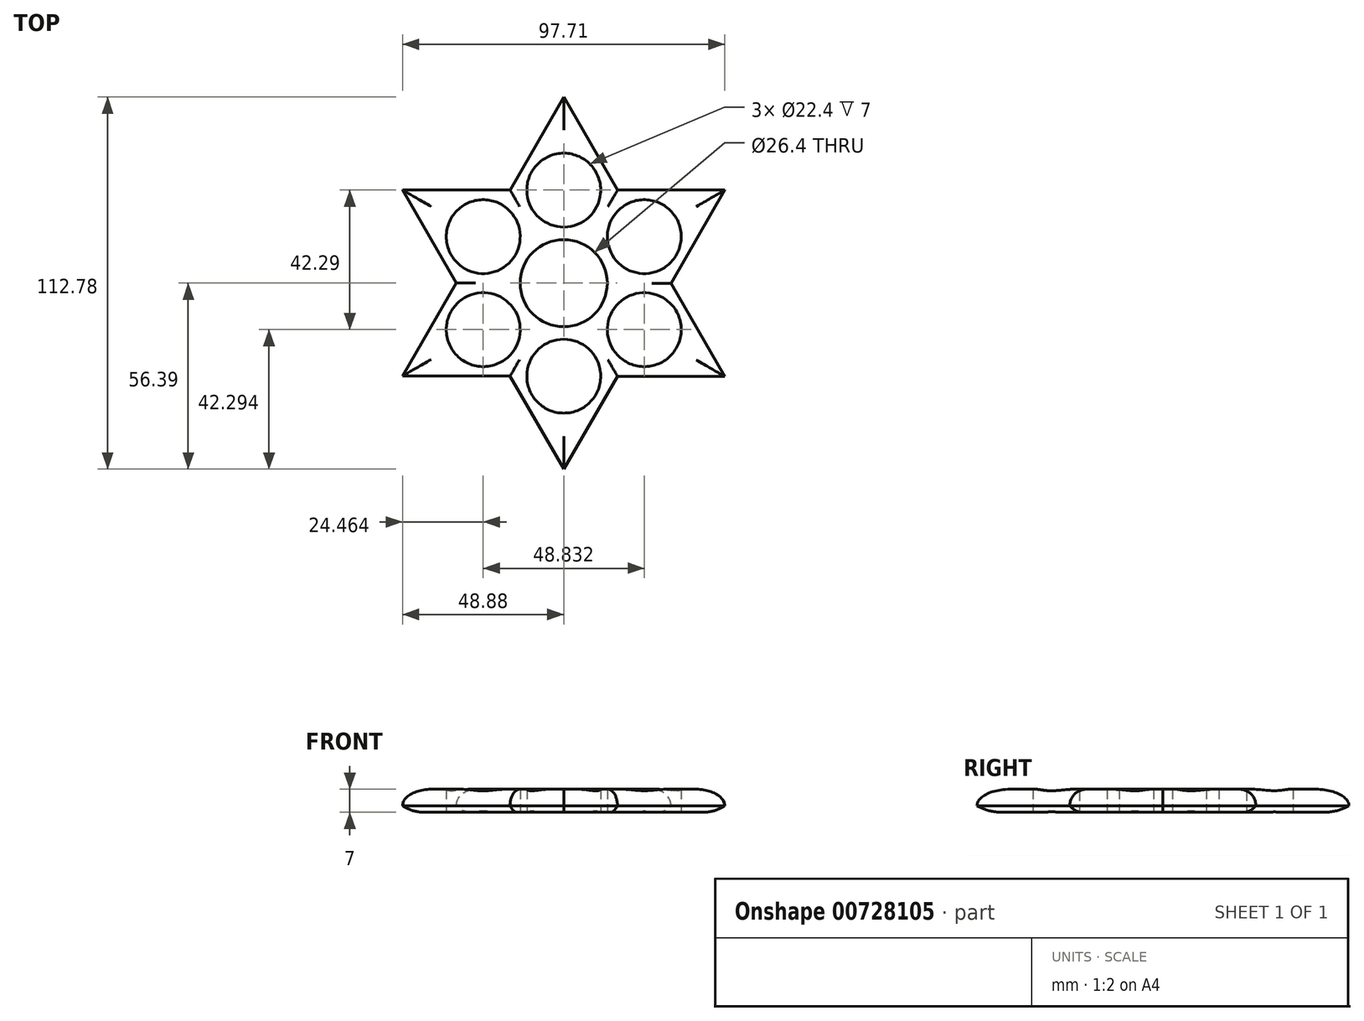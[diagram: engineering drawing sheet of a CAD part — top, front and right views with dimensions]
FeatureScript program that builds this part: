
annotation { "Feature Type Name" : "Feature", "Feature Type Description" : "" }
export const myFeature = defineFeature(function(context is Context, id is Id, definition is map)
    precondition{}
    {
        {
            var Q0;
            Q0=qCreatedBy(makeId("Top.planeOp"),FACE);
            var sketch = newSketch(context, id + "F0", { "sketchPlane" : qUnion([Q0])});
            skCircle(sketch, "E0", {"center": v(0, 0) * mm, "radius": 11.2 * mm});
            skCircle(sketch, "E1", {"center": v(0, 0) * mm, "radius": 13.2 * mm});
            skCircle(sketch, "E2.cCircle", {"center": v(0, 0) * mm, "radius": 28.2 * mm, "construction": true});
            skLineSegment(sketch, "E2.0", {"start": v(-48.83, 28.2) * mm, "end": v(48.83, 28.2) * mm});
            skLineSegment(sketch, "E2.1", {"start": v(48.83, 28.2) * mm, "end": v(0, -56.39) * mm});
            skLineSegment(sketch, "E2.2", {"start": v(0, -56.39) * mm, "end": v(-48.83, 28.2) * mm});
            skPoint(sketch, "E2.0.midPoint", {"position": v(0, 28.2) * mm});
            skLineSegment(sketch, "E3.0", {"start": v(-48.88, -28.1) * mm, "end": v(0.1, 56.39) * mm});
            skLineSegment(sketch, "E3.1", {"start": v(0.1, 56.39) * mm, "end": v(48.78, -28.28) * mm});
            skLineSegment(sketch, "E3.2", {"start": v(48.78, -28.28) * mm, "end": v(-48.88, -28.1) * mm});
            skPoint(sketch, "E3.0.midPoint", {"position": v(-24.4, 14.14) * mm});
            skCircle(sketch, "E4", {"center": v(0, 28.2) * mm, "radius": 11.2 * mm});
            skCircle(sketch, "E5.1.0", {"center": v(-24.42, 14.1) * mm, "radius": 11.2 * mm});
            skCircle(sketch, "E5.2.0", {"center": v(-24.42, -14.1) * mm, "radius": 11.2 * mm});
            skCircle(sketch, "E5.3.0", {"center": v(0, -28.2) * mm, "radius": 11.2 * mm});
            skCircle(sketch, "E5.4.0", {"center": v(24.42, -14.1) * mm, "radius": 11.2 * mm});
            skCircle(sketch, "E5.5.0", {"center": v(24.42, 14.1) * mm, "radius": 11.2 * mm});
            skSolve(sketch);
        }
        {
            var Q0;
            Q0 = qSketchRegion(id + "F0", true);
            extrude(context, id + "F1", {"entities" : qUnion([Q0]), "depth" : 7 * mm, "offsetDistance" : 25 * mm});
        }
        {
            var Q0;
            {var subQ0=sQuery(id+"F0.wireOp",EDGE,"E3.0");Q0=makeQuery(id+"F1.opExtrude","CAP_EDGE",EDGE,{"disambiguationData":[OSD([subQ0]),TDD([makeQuery(id+"F0.imprint","IMPRINT",EDGE,{"disambiguationData":[TD([[makeQuery(id+"F0.imprint","INTERSECT",VERTEX,{"derivedFrom":[subQ0,sQuery(id+"F0.wireOp",EDGE,"E3.1")]}),1.0]])],"derivedFrom":subQ0})])],"isStart":false});}
            var Q1;
            {var subQ0=sQuery(id+"F0.wireOp",EDGE,"E3.1");Q1=makeQuery(id+"F1.opExtrude","CAP_EDGE",EDGE,{"disambiguationData":[OSD([subQ0]),TDD([makeQuery(id+"F0.imprint","IMPRINT",EDGE,{"disambiguationData":[TD([[makeQuery(id+"F0.imprint","INTERSECT",VERTEX,{"derivedFrom":[sQuery(id+"F0.wireOp",EDGE,"E3.0"),subQ0]}),-1.0]])],"derivedFrom":subQ0})])],"isStart":false});}
            var Q2;
            {var subQ0=sQuery(id+"F0.wireOp",EDGE,"E2.0");Q2=makeQuery(id+"F1.opExtrude","CAP_EDGE",EDGE,{"disambiguationData":[OSD([subQ0]),TDD([makeQuery(id+"F0.imprint","IMPRINT",EDGE,{"disambiguationData":[TD([[makeQuery(id+"F0.imprint","INTERSECT",VERTEX,{"derivedFrom":[subQ0,sQuery(id+"F0.wireOp",EDGE,"E2.1")]}),1.0]])],"derivedFrom":subQ0})])],"isStart":false});}
            var Q3;
            {var subQ0=sQuery(id+"F0.wireOp",EDGE,"E2.1");Q3=makeQuery(id+"F1.opExtrude","CAP_EDGE",EDGE,{"disambiguationData":[OSD([subQ0]),TDD([makeQuery(id+"F0.imprint","IMPRINT",EDGE,{"disambiguationData":[TD([[makeQuery(id+"F0.imprint","INTERSECT",VERTEX,{"derivedFrom":[sQuery(id+"F0.wireOp",EDGE,"E2.0"),subQ0]}),-1.0]])],"derivedFrom":subQ0})])],"isStart":false});}
            var Q4;
            {var subQ0=sQuery(id+"F0.wireOp",EDGE,"E3.1");Q4=makeQuery(id+"F1.opExtrude","CAP_EDGE",EDGE,{"disambiguationData":[OSD([subQ0]),TDD([makeQuery(id+"F0.imprint","IMPRINT",EDGE,{"disambiguationData":[TD([[makeQuery(id+"F0.imprint","INTERSECT",VERTEX,{"derivedFrom":[subQ0,sQuery(id+"F0.wireOp",EDGE,"E3.2")]}),1.0]])],"derivedFrom":subQ0})])],"isStart":false});}
            var Q5;
            {var subQ0=sQuery(id+"F0.wireOp",EDGE,"E3.2");Q5=makeQuery(id+"F1.opExtrude","CAP_EDGE",EDGE,{"disambiguationData":[OSD([subQ0]),TDD([makeQuery(id+"F0.imprint","IMPRINT",EDGE,{"disambiguationData":[TD([[makeQuery(id+"F0.imprint","INTERSECT",VERTEX,{"derivedFrom":[sQuery(id+"F0.wireOp",EDGE,"E3.1"),subQ0]}),-1.0]])],"derivedFrom":subQ0})])],"isStart":false});}
            var Q6;
            {var subQ0=sQuery(id+"F0.wireOp",EDGE,"E2.1");Q6=makeQuery(id+"F1.opExtrude","CAP_EDGE",EDGE,{"disambiguationData":[OSD([subQ0]),TDD([makeQuery(id+"F0.imprint","IMPRINT",EDGE,{"disambiguationData":[TD([[makeQuery(id+"F0.imprint","INTERSECT",VERTEX,{"derivedFrom":[subQ0,sQuery(id+"F0.wireOp",EDGE,"E2.2")]}),1.0]])],"derivedFrom":subQ0})])],"isStart":false});}
            var Q7;
            {var subQ0=sQuery(id+"F0.wireOp",EDGE,"E2.2");Q7=makeQuery(id+"F1.opExtrude","CAP_EDGE",EDGE,{"disambiguationData":[OSD([subQ0]),TDD([makeQuery(id+"F0.imprint","IMPRINT",EDGE,{"disambiguationData":[TD([[makeQuery(id+"F0.imprint","INTERSECT",VERTEX,{"derivedFrom":[sQuery(id+"F0.wireOp",EDGE,"E2.1"),subQ0]}),-1.0]])],"derivedFrom":subQ0})])],"isStart":false});}
            var Q8;
            {var subQ0=sQuery(id+"F0.wireOp",EDGE,"E3.2");Q8=makeQuery(id+"F1.opExtrude","CAP_EDGE",EDGE,{"disambiguationData":[OSD([subQ0]),TDD([makeQuery(id+"F0.imprint","IMPRINT",EDGE,{"disambiguationData":[TD([[makeQuery(id+"F0.imprint","INTERSECT",VERTEX,{"derivedFrom":[sQuery(id+"F0.wireOp",EDGE,"E3.0"),subQ0]}),1.0]])],"derivedFrom":subQ0})])],"isStart":false});}
            var Q9;
            {var subQ0=sQuery(id+"F0.wireOp",EDGE,"E3.0");Q9=makeQuery(id+"F1.opExtrude","CAP_EDGE",EDGE,{"disambiguationData":[OSD([subQ0]),TDD([makeQuery(id+"F0.imprint","IMPRINT",EDGE,{"disambiguationData":[TD([[makeQuery(id+"F0.imprint","INTERSECT",VERTEX,{"derivedFrom":[subQ0,sQuery(id+"F0.wireOp",EDGE,"E3.2")]}),-1.0]])],"derivedFrom":subQ0})])],"isStart":false});}
            var Q10;
            {var subQ0=sQuery(id+"F0.wireOp",EDGE,"E2.2");Q10=makeQuery(id+"F1.opExtrude","CAP_EDGE",EDGE,{"disambiguationData":[OSD([subQ0]),TDD([makeQuery(id+"F0.imprint","IMPRINT",EDGE,{"disambiguationData":[TD([[makeQuery(id+"F0.imprint","INTERSECT",VERTEX,{"derivedFrom":[sQuery(id+"F0.wireOp",EDGE,"E2.0"),subQ0]}),1.0]])],"derivedFrom":subQ0})])],"isStart":false});}
            var Q11;
            {var subQ0=sQuery(id+"F0.wireOp",EDGE,"E2.0");Q11=makeQuery(id+"F1.opExtrude","CAP_EDGE",EDGE,{"disambiguationData":[OSD([subQ0]),TDD([makeQuery(id+"F0.imprint","IMPRINT",EDGE,{"disambiguationData":[TD([[makeQuery(id+"F0.imprint","INTERSECT",VERTEX,{"derivedFrom":[subQ0,sQuery(id+"F0.wireOp",EDGE,"E2.2")]}),-1.0]])],"derivedFrom":subQ0})])],"isStart":false});}
            fillet(context, id + "F2", {"entities" : qUnion([Q0, Q1, Q2, Q3, Q4, Q5, Q6, Q7, Q8, Q9, Q10, Q11]), "radius" : 5 * mm, "tangentPropagation" : true, "allowEdgeOverflow" : false});
        }
        {
            var Q0;
            {var subQ0=sQuery(id+"F0.wireOp",EDGE,"E2.0");Q0=makeQuery(id+"F1.opExtrude","CAP_EDGE",EDGE,{"disambiguationData":[OSD([subQ0]),TDD([makeQuery(id+"F0.imprint","IMPRINT",EDGE,{"disambiguationData":[TD([[makeQuery(id+"F0.imprint","INTERSECT",VERTEX,{"derivedFrom":[subQ0,sQuery(id+"F0.wireOp",EDGE,"E2.1")]}),1.0]])],"derivedFrom":subQ0})])],"isStart":true});}
            var Q1;
            {var subQ0=sQuery(id+"F0.wireOp",EDGE,"E2.1");Q1=makeQuery(id+"F1.opExtrude","CAP_EDGE",EDGE,{"disambiguationData":[OSD([subQ0]),TDD([makeQuery(id+"F0.imprint","IMPRINT",EDGE,{"disambiguationData":[TD([[makeQuery(id+"F0.imprint","INTERSECT",VERTEX,{"derivedFrom":[sQuery(id+"F0.wireOp",EDGE,"E2.0"),subQ0]}),-1.0]])],"derivedFrom":subQ0})])],"isStart":true});}
            var Q2;
            {var subQ0=sQuery(id+"F0.wireOp",EDGE,"E3.1");Q2=makeQuery(id+"F1.opExtrude","CAP_EDGE",EDGE,{"disambiguationData":[OSD([subQ0]),TDD([makeQuery(id+"F0.imprint","IMPRINT",EDGE,{"disambiguationData":[TD([[makeQuery(id+"F0.imprint","INTERSECT",VERTEX,{"derivedFrom":[subQ0,sQuery(id+"F0.wireOp",EDGE,"E3.2")]}),1.0]])],"derivedFrom":subQ0})])],"isStart":true});}
            var Q3;
            {var subQ0=sQuery(id+"F0.wireOp",EDGE,"E3.2");Q3=makeQuery(id+"F1.opExtrude","CAP_EDGE",EDGE,{"disambiguationData":[OSD([subQ0]),TDD([makeQuery(id+"F0.imprint","IMPRINT",EDGE,{"disambiguationData":[TD([[makeQuery(id+"F0.imprint","INTERSECT",VERTEX,{"derivedFrom":[sQuery(id+"F0.wireOp",EDGE,"E3.1"),subQ0]}),-1.0]])],"derivedFrom":subQ0})])],"isStart":true});}
            var Q4;
            {var subQ0=sQuery(id+"F0.wireOp",EDGE,"E2.1");Q4=makeQuery(id+"F1.opExtrude","CAP_EDGE",EDGE,{"disambiguationData":[OSD([subQ0]),TDD([makeQuery(id+"F0.imprint","IMPRINT",EDGE,{"disambiguationData":[TD([[makeQuery(id+"F0.imprint","INTERSECT",VERTEX,{"derivedFrom":[subQ0,sQuery(id+"F0.wireOp",EDGE,"E2.2")]}),1.0]])],"derivedFrom":subQ0})])],"isStart":true});}
            var Q5;
            {var subQ0=sQuery(id+"F0.wireOp",EDGE,"E2.2");Q5=makeQuery(id+"F1.opExtrude","CAP_EDGE",EDGE,{"disambiguationData":[OSD([subQ0]),TDD([makeQuery(id+"F0.imprint","IMPRINT",EDGE,{"disambiguationData":[TD([[makeQuery(id+"F0.imprint","INTERSECT",VERTEX,{"derivedFrom":[sQuery(id+"F0.wireOp",EDGE,"E2.1"),subQ0]}),-1.0]])],"derivedFrom":subQ0})])],"isStart":true});}
            var Q6;
            {var subQ0=sQuery(id+"F0.wireOp",EDGE,"E3.2");Q6=makeQuery(id+"F1.opExtrude","CAP_EDGE",EDGE,{"disambiguationData":[OSD([subQ0]),TDD([makeQuery(id+"F0.imprint","IMPRINT",EDGE,{"disambiguationData":[TD([[makeQuery(id+"F0.imprint","INTERSECT",VERTEX,{"derivedFrom":[sQuery(id+"F0.wireOp",EDGE,"E3.0"),subQ0]}),1.0]])],"derivedFrom":subQ0})])],"isStart":true});}
            var Q7;
            {var subQ0=sQuery(id+"F0.wireOp",EDGE,"E3.0");Q7=makeQuery(id+"F1.opExtrude","CAP_EDGE",EDGE,{"disambiguationData":[OSD([subQ0]),TDD([makeQuery(id+"F0.imprint","IMPRINT",EDGE,{"disambiguationData":[TD([[makeQuery(id+"F0.imprint","INTERSECT",VERTEX,{"derivedFrom":[subQ0,sQuery(id+"F0.wireOp",EDGE,"E3.2")]}),-1.0]])],"derivedFrom":subQ0})])],"isStart":true});}
            var Q8;
            {var subQ0=sQuery(id+"F0.wireOp",EDGE,"E2.2");Q8=makeQuery(id+"F1.opExtrude","CAP_EDGE",EDGE,{"disambiguationData":[OSD([subQ0]),TDD([makeQuery(id+"F0.imprint","IMPRINT",EDGE,{"disambiguationData":[TD([[makeQuery(id+"F0.imprint","INTERSECT",VERTEX,{"derivedFrom":[sQuery(id+"F0.wireOp",EDGE,"E2.0"),subQ0]}),1.0]])],"derivedFrom":subQ0})])],"isStart":true});}
            var Q9;
            {var subQ0=sQuery(id+"F0.wireOp",EDGE,"E2.0");Q9=makeQuery(id+"F1.opExtrude","CAP_EDGE",EDGE,{"disambiguationData":[OSD([subQ0]),TDD([makeQuery(id+"F0.imprint","IMPRINT",EDGE,{"disambiguationData":[TD([[makeQuery(id+"F0.imprint","INTERSECT",VERTEX,{"derivedFrom":[subQ0,sQuery(id+"F0.wireOp",EDGE,"E2.2")]}),-1.0]])],"derivedFrom":subQ0})])],"isStart":true});}
            var Q10;
            {var subQ0=sQuery(id+"F0.wireOp",EDGE,"E3.1");Q10=makeQuery(id+"F1.opExtrude","CAP_EDGE",EDGE,{"disambiguationData":[OSD([subQ0]),TDD([makeQuery(id+"F0.imprint","IMPRINT",EDGE,{"disambiguationData":[TD([[makeQuery(id+"F0.imprint","INTERSECT",VERTEX,{"derivedFrom":[sQuery(id+"F0.wireOp",EDGE,"E3.0"),subQ0]}),-1.0]])],"derivedFrom":subQ0})])],"isStart":true});}
            var Q11;
            {var subQ0=sQuery(id+"F0.wireOp",EDGE,"E3.0");Q11=makeQuery(id+"F1.opExtrude","CAP_EDGE",EDGE,{"disambiguationData":[OSD([subQ0]),TDD([makeQuery(id+"F0.imprint","IMPRINT",EDGE,{"disambiguationData":[TD([[makeQuery(id+"F0.imprint","INTERSECT",VERTEX,{"derivedFrom":[subQ0,sQuery(id+"F0.wireOp",EDGE,"E3.1")]}),1.0]])],"derivedFrom":subQ0})])],"isStart":true});}
            fillet(context, id + "F3", {"entities" : qUnion([Q0, Q1, Q2, Q3, Q4, Q5, Q6, Q7, Q8, Q9, Q10, Q11]), "radius" : 5 * mm, "tangentPropagation" : true, "allowEdgeOverflow" : false});
        }
    });
